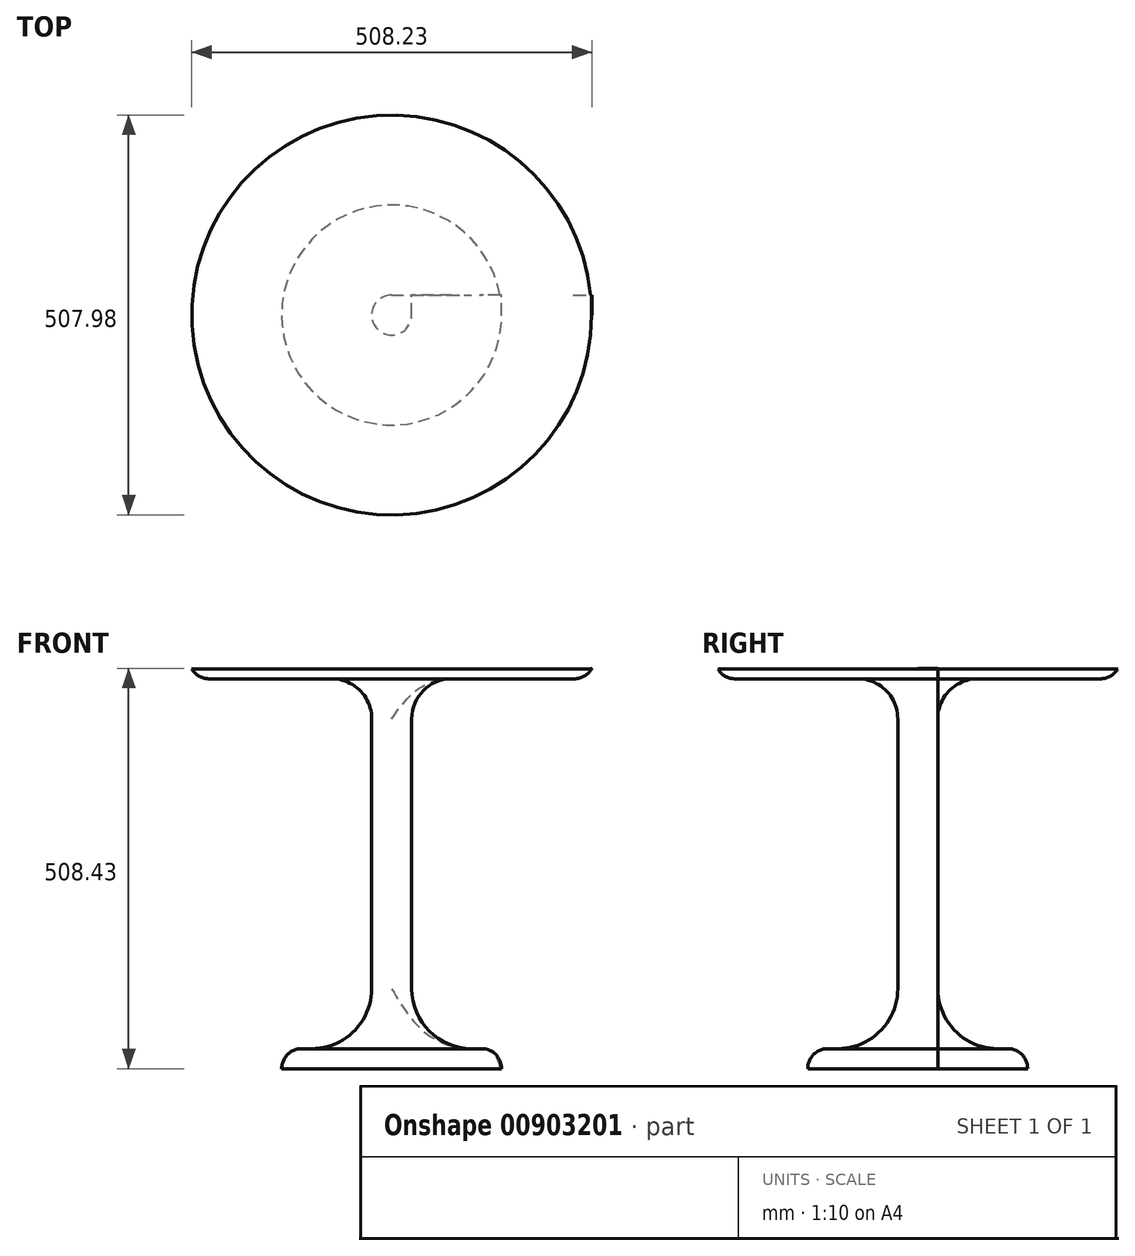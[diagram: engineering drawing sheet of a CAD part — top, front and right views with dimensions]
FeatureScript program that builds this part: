
annotation { "Feature Type Name" : "Feature", "Feature Type Description" : "" }
export const myFeature = defineFeature(function(context is Context, id is Id, definition is map)
    precondition{}
    {
        {
            var Q0;
            Q0=qCreatedBy(makeId("Front.planeOp"),FACE);
            var sketch = newSketch(context, id + "F0", { "sketchPlane" : qUnion([Q0])});
            skLineSegment(sketch, "E0", {"start": v(0, 0) * mm, "end": v(139.7, 0) * mm});
            skLineSegment(sketch, "E1", {"start": v(0, 508) * mm, "end": v(254, 508) * mm});
            skLineSegment(sketch, "E2", {"start": v(0, 0) * mm, "end": v(0, 508) * mm});
            skLineSegment(sketch, "E3", {"start": v(25.4, 444.5) * mm, "end": v(25.4, 101.6) * mm});
            skLineSegment(sketch, "E4", {"start": v(76.2, 495.3) * mm, "end": v(232, 495.3) * mm});
            skLineSegment(sketch, "E5", {"start": v(254.24, 508.43) * mm, "end": v(254, 508) * mm});
            skLineSegment(sketch, "E6", {"start": v(101.6, 25.4) * mm, "end": v(114.3, 25.4) * mm});
            skLineSegment(sketch, "E7", {"start": v(139.7, 0) * mm, "end": v(139.7, 0) * mm});
            skPoint(sketch, "E8.visualSharp", {"position": v(25.4, 495.3) * mm});
            skArc(sketch, "E8.filletArc", {"start": v(76.2, 495.3) * mm, "mid": v(40.28, 480.42) * mm, "end": v(25.4, 444.5) * mm});
            skPoint(sketch, "E9.visualSharp", {"position": v(25.4, 25.4) * mm});
            skArc(sketch, "E9.filletArc", {"start": v(25.4, 101.6) * mm, "mid": v(47.72, 47.72) * mm, "end": v(101.6, 25.4) * mm});
            skPoint(sketch, "E10.visualSharp", {"position": v(139.7, 25.4) * mm});
            skArc(sketch, "E10.filletArc", {"start": v(139.7, 0) * mm, "mid": v(132.26, 17.96) * mm, "end": v(114.3, 25.4) * mm});
            skPoint(sketch, "E11.visualSharp", {"position": v(247, 495.3) * mm});
            skArc(sketch, "E11.filletArc", {"start": v(232, 495.3) * mm, "mid": v(244.91, 498.83) * mm, "end": v(254.24, 508.43) * mm});
            skSolve(sketch);
        }
        {
            var Q0;
            Q0 = qSketchRegion(id + "F0", true);
            extrude(context, id + "F1", {"entities" : qUnion([Q0]), "depth" : 25.4 * mm, "offsetDistance" : 25.4 * mm});
        }
        {
            var Q0;
            Q0=makeQuery(id+"F1.opExtrude","CAP_FACE",FACE,{"disambiguationData":[OSD([sQuery(id+"F0.wireOp",EDGE,"E0"),sQuery(id+"F0.wireOp",EDGE,"E1"),sQuery(id+"F0.wireOp",EDGE,"E2"),sQuery(id+"F0.wireOp",EDGE,"E3"),sQuery(id+"F0.wireOp",EDGE,"E4"),sQuery(id+"F0.wireOp",EDGE,"E6"),sQuery(id+"F0.wireOp",EDGE,"E8.filletArc"),sQuery(id+"F0.wireOp",EDGE,"E9.filletArc"),sQuery(id+"F0.wireOp",EDGE,"E10.filletArc"),sQuery(id+"F0.wireOp",EDGE,"E11.filletArc")])],"isStart":false});
            var Q1;
            Q1=makeQuery(id+"F1.opExtrude","CAP_EDGE",EDGE,{"disambiguationData":[OSD([sQuery(id+"F0.wireOp",EDGE,"E2")])],"isStart":false});
            revolve(context, id + "F2", {"operationType" : NewBodyOperationType.ADD, "surfaceOperationType" : NewSurfaceOperationType.NEW, "entities" : qUnion([Q0]), "axis" : qUnion([Q1]), "revolveType" : RevolveType.FULL});
        }
    });
